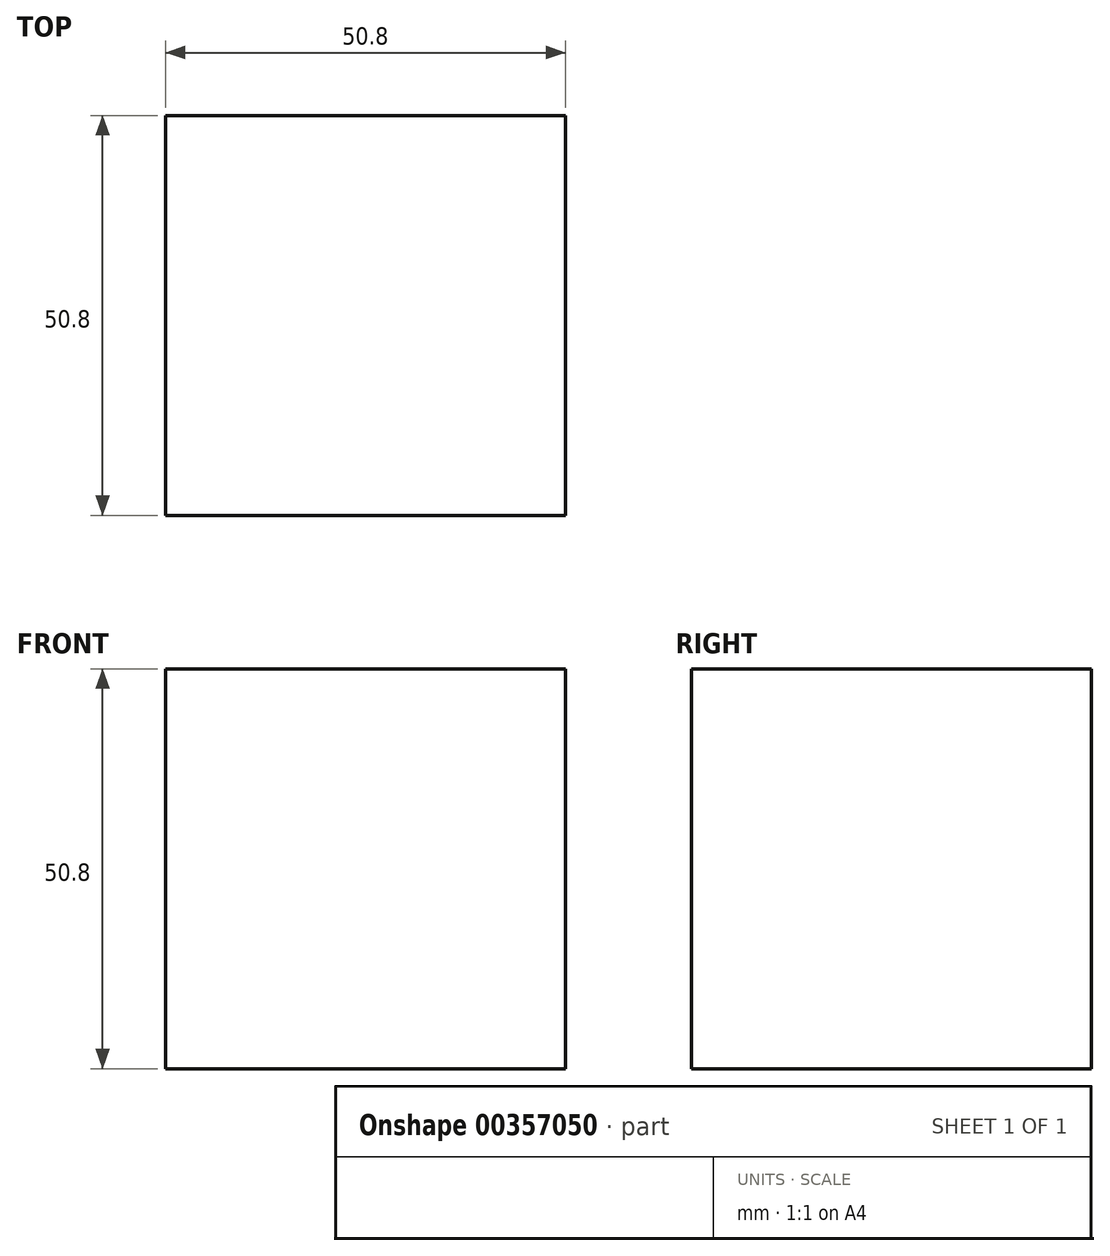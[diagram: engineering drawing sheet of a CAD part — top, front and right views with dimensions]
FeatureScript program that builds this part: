
annotation { "Feature Type Name" : "Feature", "Feature Type Description" : "" }
export const myFeature = defineFeature(function(context is Context, id is Id, definition is map)
    precondition{}
    {
        {
            var Q0;
            Q0=qCreatedBy(makeId("Front.planeOp"),FACE);
            var sketch = newSketch(context, id + "F0", { "sketchPlane" : qUnion([Q0])});
            skLineSegment(sketch, "E0", {"start": v(0, 0) * mm, "end": v(0, 50.8) * mm});
            skLineSegment(sketch, "E1", {"start": v(0, 50.8) * mm, "end": v(50.8, 50.8) * mm});
            skLineSegment(sketch, "E2", {"start": v(50.8, 50.8) * mm, "end": v(50.8, 0) * mm});
            skLineSegment(sketch, "E3", {"start": v(50.8, 0) * mm, "end": v(0, 0) * mm});
            skSolve(sketch);
        }
        {
            var Q0;
            Q0 = qSketchRegion(id + "F0", true);
            extrude(context, id + "F1", {"entities" : qUnion([Q0]), "depth" : 50.8 * mm});
        }
    });
